# Revit family: 3D BIM Model TurboMAG Quadplex (Skid) 2017
name_source: partatom
category: Plumbing Fixtures
revit_build: Autodesk Revit 2017 (Build: 20160225_1515(x64)
units: mm (PartAtom-declared; Revit-internal decimal feet)

## family parameters
Always vertical = Yes
Cut with Voids When Loaded = No
OmniClass Number = 23.45.00.00
OmniClass Title = Sanitary, Laundry, and Cleaning Equipment
Part Type = Normal
Room Calculation Point = No
Round Connector Dimension = Use Radius
Shared = No
Work Plane-Based = No

## types (1)
- Quadplex Skid
    A = 50 mm  [stored 0.164042 ft]
    Frame = Steel, Paint Finish, Blue
    I/O OR = 30 mm  [stored 0.0984252 ft]
    I/O Pipe R = 25 mm  [stored 0.082021 ft]
    I/O Pipe t = 5 mm  [stored 0.0164042 ft]
    Manufacturer = Hydrotec
    Manufacturer website = http://www.hydrotec.co.uk
    Model = Hydromag T-Quadplex (skid)
    Nominal flow = 2.3 L/s
    P_OR = 14 mm  [stored 0.0459318 ft]
    Pipe = Iron, Gray Cast ASTM A48 Grade 30
    Product Category = Scale Control
    Service weight = 145.00 kg
    Skid frame width = 40 mm  [stored 0.131234 ft]
    Skid height = 935 mm
    Skid length = 760 mm
    Skid width = 1120 mm  [stored 3.67454 ft]
    Switch box = UHMW, White
    Vent Connection = No
    Waste Connection = No

note: [stored X ft] marks values corroborated as IEEE doubles in the binary element streams (Revit-internal decimal feet)

## geometry (parser evidence)
native form markers: Blend x22, Sweep x23
no freeform markers — native parametric forms only
